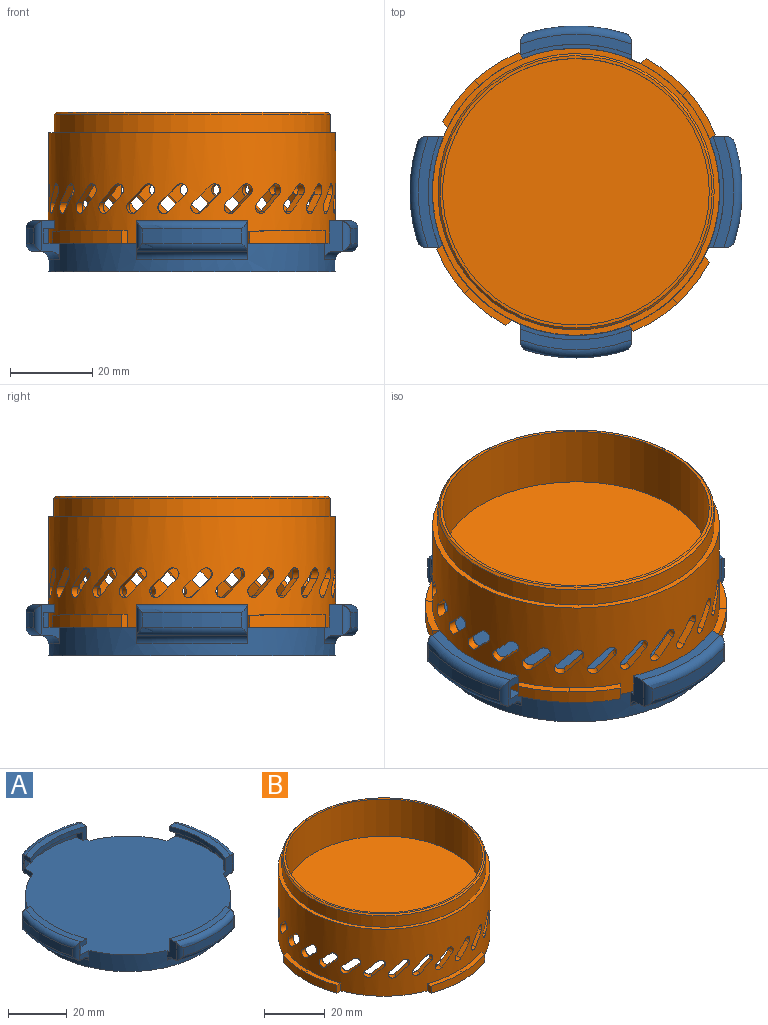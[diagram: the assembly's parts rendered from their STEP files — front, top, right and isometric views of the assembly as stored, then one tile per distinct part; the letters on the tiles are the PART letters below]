
ASSEMBLY  parts=2 mates=1
PART A: 62 faces, bbox 87.7x87.7x12.5 mm
  f0: cylinder r=35mm len=70mm, axis (0,0,-1), area 1095.9mm2, adj f1,f3,f7,f8,f19,f21,f22,f33
  f1: plane 77.24x77.24mm, normal (0,0,1), area 4232.4mm2, adj f0,f7,f8,f10,f11,f12,f21,f22
  f2: cylinder r=33.75mm len=67.5mm, axis (0,0,-1), area 954.3mm2, adj f4,f5
  f3: plane 70x70mm, normal (0,0,-1), area 163.2mm2, adj f0,f5
  f4: plane 67.5x67.5mm, normal (0,0,-1), area 3578.5mm2, adj f2
  f5: cone r=34.25mm half-angle=45deg, axis (0,0,-1), area 151.1mm2, adj f2,f3
  f6: cylinder r=40.5mm len=24.2mm, axis (0,0,1), area 86mm2, adj f15,f16,f17,f18
  f7: plane 9.51x4.46mm, normal (0,-1,0), area 18.4mm2, adj f0,f1,f9,f10,f12,f13,f14,f15
  f8: plane 9.51x4.46mm, normal (0,1,0), area 28mm2, adj f0,f1,f9,f12,f13,f15,f16,f18
  f9: plane 27x4.05mm, normal (0,0,-1), area 41.4mm2, adj f7,f8,f15,f19
  f10: cylinder r=38.62mm len=25.5mm, axis (0,0,-1), area 91mm2, adj f1,f7,f11,f14
  f11: plane 3.5x2.71mm, normal (0,-1,0), area 9.5mm2, adj f1,f10,f12,f14
  f12: cylinder r=36.06mm len=27mm, axis (0,0,-1), area 61mm2, adj f1,f7,f8,f11,f13,f14
  f13: plane 27x5.07mm, normal (0,0,1), area 67.5mm2, adj f7,f8,f12,f18
  f14: plane 25.5x5.19mm, normal (0,0,-1), area 66.7mm2, adj f7,f10,f11,f12
  f15: torus R=38.5mm, axis (0,0,1), area 84mm2, adj f6,f7,f8,f9,f16,f17
  f16: cylinder r=2mm len=7.29mm, axis (0,0,1), area 14.4mm2, adj f6,f8,f15,f18
  f17: cylinder r=2mm len=7.29mm, axis (0,0,1), area 14.4mm2, adj f6,f7,f15,f18
  f18: torus R=38.5mm, axis (0,0,1), area 84mm2, adj f6,f7,f8,f13,f16,f17
  f19: torus R=37mm, axis (0,0,1), area 87mm2, adj f0,f7,f8,f9
  f20: cylinder r=40.5mm len=24.2mm, axis (0,0,1), area 86mm2, adj f29,f30,f31,f32
  f21: plane 9.51x4.46mm, normal (-1,0,0), area 18.4mm2, adj f0,f1,f23,f24,f26,f27,f28,f29
  f22: plane 9.51x4.46mm, normal (1,0,0), area 28mm2, adj f0,f1,f23,f26,f27,f29,f30,f32
  f23: plane 27x4.05mm, normal (0,0,-1), area 41.4mm2, adj f21,f22,f29,f33
  f24: cylinder r=38.62mm len=25.5mm, axis (0,0,-1), area 91mm2, adj f1,f21,f25,f28
  f25: plane 3.5x2.71mm, normal (-1,0,0), area 9.5mm2, adj f1,f24,f26,f28
  f26: cylinder r=36.06mm len=27mm, axis (0,0,-1), area 61mm2, adj f1,f21,f22,f25,f27,f28
  f27: plane 27x5.07mm, normal (0,0,1), area 67.5mm2, adj f21,f22,f26,f32
  f28: plane 25.5x5.19mm, normal (0,0,-1), area 66.7mm2, adj f21,f24,f25,f26
  f29: torus R=38.5mm, axis (0,0,1), area 84mm2, adj f20,f21,f22,f23,f30,f31
  f30: cylinder r=2mm len=7.29mm, axis (0,0,1), area 14.4mm2, adj f20,f22,f29,f32
  f31: cylinder r=2mm len=7.29mm, axis (0,0,1), area 14.4mm2, adj f20,f21,f29,f32
  f32: torus R=38.5mm, axis (0,0,1), area 84mm2, adj f20,f21,f22,f27,f30,f31
  f33: torus R=37mm, axis (0,0,1), area 87mm2, adj f0,f21,f22,f23
  f34: cylinder r=40.5mm len=24.2mm, axis (0,0,1), area 86mm2, adj f43,f44,f45,f46
  f35: plane 9.51x4.46mm, normal (0,1,0), area 18.4mm2, adj f0,f1,f37,f38,f40,f41,f42,f43
  f36: plane 9.51x4.46mm, normal (0,-1,0), area 28mm2, adj f0,f1,f37,f40,f41,f43,f44,f46
  f37: plane 27x4.05mm, normal (0,0,-1), area 41.4mm2, adj f35,f36,f43,f47
  f38: cylinder r=38.62mm len=25.5mm, axis (0,0,-1), area 91mm2, adj f1,f35,f39,f42
  f39: plane 3.5x2.71mm, normal (0,1,0), area 9.5mm2, adj f1,f38,f40,f42
  f40: cylinder r=36.06mm len=27mm, axis (0,0,-1), area 61mm2, adj f1,f35,f36,f39,f41,f42
  f41: plane 27x5.07mm, normal (0,0,1), area 67.5mm2, adj f35,f36,f40,f46
  f42: plane 25.5x5.19mm, normal (0,0,-1), area 66.7mm2, adj f35,f38,f39,f40
  f43: torus R=38.5mm, axis (0,0,1), area 84mm2, adj f34,f35,f36,f37,f44,f45
  f44: cylinder r=2mm len=7.29mm, axis (0,0,1), area 14.4mm2, adj f34,f36,f43,f46
  f45: cylinder r=2mm len=7.29mm, axis (0,0,1), area 14.4mm2, adj f34,f35,f43,f46
  f46: torus R=38.5mm, axis (0,0,1), area 84mm2, adj f34,f35,f36,f41,f44,f45
  f47: torus R=37mm, axis (0,0,1), area 87mm2, adj f0,f35,f36,f37
  f48: cylinder r=40.5mm len=24.2mm, axis (0,0,1), area 86mm2, adj f57,f58,f59,f60
  f49: plane 9.51x4.46mm, normal (1,0,0), area 18.4mm2, adj f0,f1,f51,f52,f54,f55,f56,f57
  f50: plane 9.51x4.46mm, normal (-1,0,0), area 28mm2, adj f0,f1,f51,f54,f55,f57,f58,f60
  f51: plane 27x4.05mm, normal (0,0,-1), area 41.4mm2, adj f49,f50,f57,f61
  f52: cylinder r=38.62mm len=25.5mm, axis (0,0,-1), area 91mm2, adj f1,f49,f53,f56
  f53: plane 3.5x2.71mm, normal (1,0,0), area 9.5mm2, adj f1,f52,f54,f56
  f54: cylinder r=36.06mm len=27mm, axis (0,0,-1), area 61mm2, adj f1,f49,f50,f53,f55,f56
  f55: plane 27x5.07mm, normal (0,0,1), area 67.5mm2, adj f49,f50,f54,f60
  f56: plane 25.5x5.19mm, normal (0,0,-1), area 66.7mm2, adj f49,f52,f53,f54
  f57: torus R=38.5mm, axis (0,0,1), area 84mm2, adj f48,f49,f50,f51,f58,f59
  f58: cylinder r=2mm len=7.29mm, axis (0,0,1), area 14.4mm2, adj f48,f50,f57,f60
  f59: cylinder r=2mm len=7.29mm, axis (0,0,1), area 14.4mm2, adj f48,f49,f57,f60
  f60: torus R=38.5mm, axis (0,0,1), area 84mm2, adj f48,f49,f50,f55,f58,f59
  f61: torus R=37mm, axis (0,0,1), area 87mm2, adj f0,f49,f50,f51
PART B: 138 faces, bbox 73.5x73.5x32 mm
  f0: cylinder r=35mm len=70mm, axis (0,0,-1), area 4937.3mm2, adj f5,f8,f11,f12,f13,f14,f16,f17
  f1: plane 66.38x66.38mm, normal (0,0,1), area 142.4mm2, adj f2,f6
  f2: cylinder r=32.5mm len=65mm, axis (0,0,-1), area 3063.1mm2, adj f1,f3
  f3: plane 65x65mm, normal (0,0,1), area 3318.3mm2, adj f2
  f4: cylinder r=33.69mm len=67.38mm, axis (0,0,1), area 952.6mm2, adj f5,f6
  f5: plane 70x70mm, normal (0,0,1), area 282.7mm2, adj f0,f4
  f6: cone r=33.19mm half-angle=45deg, axis (0,0,-1), area 148.6mm2, adj f1,f4
  f7: cylinder r=33mm len=66mm, axis (0,0,1), area 2432.3mm2, adj f8,f9,f26,f27,f28,f29,f30,f31
  f8: plane 73.5x73.5mm, normal (0,0,-1), area 606mm2, adj f0,f7,f10,f11,f12,f14,f15,f16
  f9: plane 66x66mm, normal (0,0,-1), area 3421.2mm2, adj f7
  f10: cylinder r=36.75mm len=25mm, axis (0,0,-1), area 79.7mm2, adj f8,f11,f12,f13,f134
  f11: plane 2.9x1.87mm, normal (-1,0,0), area 5.4mm2, adj f0,f8,f10,f134
  f12: plane 3.2x1.87mm, normal (1,0,0), area 6mm2, adj f0,f8,f10,f13
  f13: plane 12.5x4.06mm, normal (0,0,1), area 22.3mm2, adj f0,f10,f12,f134
  f14: plane 3.2x1.87mm, normal (0,-1,0), area 6mm2, adj f0,f8,f15,f17
  f15: cylinder r=36.75mm len=25mm, axis (0,0,-1), area 79.7mm2, adj f8,f14,f16,f17,f137
  f16: plane 2.9x1.87mm, normal (0,1,0), area 5.4mm2, adj f0,f8,f15,f137
  f17: plane 12.5x4.06mm, normal (0,0,1), area 22.3mm2, adj f0,f14,f15,f137
  f18: plane 3.2x1.87mm, normal (-1,0,0), area 6mm2, adj f0,f8,f19,f21
  f19: cylinder r=36.75mm len=25mm, axis (0,0,-1), area 79.7mm2, adj f8,f18,f20,f21,f136
  f20: plane 2.9x1.87mm, normal (1,0,0), area 5.4mm2, adj f0,f8,f19,f136
  f21: plane 12.5x4.06mm, normal (0,0,1), area 22.3mm2, adj f0,f18,f19,f136
  f22: plane 3.2x1.87mm, normal (0,1,0), area 6mm2, adj f0,f8,f23,f25
  f23: cylinder r=36.75mm len=25mm, axis (0,0,-1), area 79.7mm2, adj f8,f22,f24,f25,f135
  f24: plane 2.9x1.87mm, normal (0,-1,0), area 5.4mm2, adj f0,f8,f23,f135
  f25: plane 12.5x4.06mm, normal (0,0,1), area 22.3mm2, adj f0,f22,f23,f135
  f26: cylinder r=1.5mm len=2.56mm, axis (0,-1,0), area 9.4mm2, adj f0,f7,f27,f29
  f27: plane 4.18x4.18mm, normal (0.71,0,0.71), area 11.8mm2, adj f0,f7,f26,f28
  f28: cylinder r=1.5mm len=2.62mm, axis (0,-1,0), area 9.7mm2, adj f0,f7,f27,f29
  f29: plane 4.26x4.26mm, normal (-0.71,0,-0.71), area 12.1mm2, adj f0,f7,f26,f28
  f30: cylinder r=1.5mm len=2.95mm, axis (-0.23,-0.97,0), area 9.4mm2, adj f0,f7,f31,f33
  f31: plane 4.5x4.18mm, normal (0.69,-0.16,0.71), area 11.8mm2, adj f0,f7,f30,f32
  f32: cylinder r=1.5mm len=3.1mm, axis (-0.23,-0.97,0), area 9.7mm2, adj f0,f7,f31,f33
  f33: plane 4.51x4.26mm, normal (-0.69,0.16,-0.71), area 12.1mm2, adj f0,f7,f30,f32
  f34: cylinder r=1.5mm len=3.19mm, axis (-0.45,-0.89,0), area 9.4mm2, adj f0,f7,f35,f37
  f35: plane 4.58x4.18mm, normal (0.63,-0.32,0.71), area 11.8mm2, adj f0,f7,f34,f36
  f36: cylinder r=1.5mm len=3.41mm, axis (-0.45,-0.89,0), area 9.7mm2, adj f0,f7,f35,f37
  f37: plane 4.53x4.26mm, normal (-0.63,0.32,-0.71), area 12.1mm2, adj f0,f7,f34,f36
  f38: cylinder r=1.5mm len=3.25mm, axis (-0.64,-0.77,0), area 9.4mm2, adj f0,f7,f39,f41
  f39: plane 4.41x4.32mm, normal (0.54,-0.45,0.71), area 11.8mm2, adj f0,f7,f38,f40
  f40: cylinder r=1.5mm len=3.53mm, axis (-0.64,-0.77,0), area 9.7mm2, adj f0,f7,f39,f41
  f41: plane 4.59x4.3mm, normal (-0.54,0.45,-0.71), area 12.1mm2, adj f0,f7,f38,f40
  f42: cylinder r=1.5mm len=3.25mm, axis (-0.8,-0.6,0), area 9.4mm2, adj f0,f7,f43,f45
  f43: plane 4.63x4.18mm, normal (0.42,-0.57,0.71), area 11.8mm2, adj f0,f7,f42,f44
  f44: cylinder r=1.5mm len=3.52mm, axis (-0.8,-0.6,0), area 9.7mm2, adj f0,f7,f43,f45
  f45: plane 4.86x4.26mm, normal (-0.42,0.57,-0.71), area 12.1mm2, adj f0,f7,f42,f44
  f46: cylinder r=1.5mm len=3.14mm, axis (-0.92,-0.4,0), area 9.4mm2, adj f0,f7,f47,f49
  f47: plane 4.69x4.18mm, normal (0.28,-0.65,0.71), area 11.8mm2, adj f0,f7,f46,f48
  f48: cylinder r=1.5mm len=3.35mm, axis (-0.92,-0.4,0), area 9.7mm2, adj f0,f7,f47,f49
  f49: plane 4.86x4.26mm, normal (-0.28,0.65,-0.71), area 12.1mm2, adj f0,f7,f46,f48
  f50: cylinder r=1.5mm len=2.87mm, axis (-0.98,-0.17,0), area 9.4mm2, adj f0,f7,f51,f53
  f51: plane 4.49x4.18mm, normal (0.12,-0.7,0.71), area 11.8mm2, adj f0,f7,f50,f52
  f52: cylinder r=1.5mm len=2.99mm, axis (-0.98,-0.17,0), area 9.7mm2, adj f0,f7,f51,f53
  f53: plane 4.61x4.26mm, normal (-0.12,0.7,-0.71), area 12.1mm2, adj f0,f7,f50,f52
  f54: cylinder r=1.5mm len=2.67mm, axis (-1,0.06,0), area 9.4mm2, adj f0,f7,f55,f57
  f55: plane 4.29x4.18mm, normal (-0.04,-0.71,0.71), area 11.8mm2, adj f0,f7,f54,f56
  f56: cylinder r=1.5mm len=2.76mm, axis (-1,0.06,0), area 9.7mm2, adj f0,f7,f55,f57
  f57: plane 4.34x4.26mm, normal (0.04,0.71,-0.71), area 12.1mm2, adj f0,f7,f54,f56
  f58: cylinder r=1.5mm len=3.03mm, axis (-0.96,0.29,0), area 9.4mm2, adj f0,f7,f59,f61
  f59: plane 4.55x4.18mm, normal (-0.2,-0.68,0.71), area 11.8mm2, adj f0,f7,f58,f60
  f60: cylinder r=1.5mm len=3.19mm, axis (-0.96,0.29,0), area 9.7mm2, adj f0,f7,f59,f61
  f61: plane 4.54x4.26mm, normal (0.2,0.68,-0.71), area 12.1mm2, adj f0,f7,f58,f60
  f62: cylinder r=1.5mm len=3.22mm, axis (-0.87,0.5,0), area 9.4mm2, adj f0,f7,f63,f65
  f63: plane 4.56x4.18mm, normal (-0.35,-0.61,0.71), area 11.8mm2, adj f0,f7,f62,f64
  f64: cylinder r=1.5mm len=3.45mm, axis (-0.87,0.5,0), area 9.7mm2, adj f0,f7,f63,f65
  f65: plane 4.49x4.26mm, normal (0.35,0.61,-0.71), area 12.1mm2, adj f0,f7,f62,f64
  f66: cylinder r=1.5mm len=3.24mm, axis (-0.73,0.69,0), area 9.4mm2, adj f0,f7,f67,f69
  f67: plane 4.42x4.33mm, normal (-0.49,-0.51,0.71), area 11.8mm2, adj f0,f7,f66,f68
  f68: cylinder r=1.5mm len=3.53mm, axis (-0.73,0.69,0), area 9.7mm2, adj f0,f7,f67,f69
  f69: plane 4.68x4.26mm, normal (0.49,0.51,-0.71), area 12.1mm2, adj f0,f7,f66,f68
  f70: cylinder r=1.5mm len=3.24mm, axis (-0.55,0.84,0), area 9.4mm2, adj f0,f7,f71,f73
  f71: plane 4.67x4.18mm, normal (-0.59,-0.39,0.71), area 11.8mm2, adj f0,f7,f70,f72
  f72: cylinder r=1.5mm len=3.49mm, axis (-0.55,0.84,0), area 9.7mm2, adj f0,f7,f71,f73
  f73: plane 4.88x4.26mm, normal (0.59,0.39,-0.71), area 12.1mm2, adj f0,f7,f70,f72
  f74: cylinder r=1.5mm len=3.09mm, axis (-0.34,0.94,0), area 9.4mm2, adj f0,f7,f75,f77
  f75: plane 4.66x4.18mm, normal (-0.66,-0.24,0.71), area 11.8mm2, adj f0,f7,f74,f76
  f76: cylinder r=1.5mm len=3.27mm, axis (-0.34,0.94,0), area 9.7mm2, adj f0,f7,f75,f77
  f77: plane 4.83x4.26mm, normal (0.66,0.24,-0.71), area 12.1mm2, adj f0,f7,f74,f76
  f78: cylinder r=1.5mm len=2.78mm, axis (-0.12,0.99,0), area 9.4mm2, adj f0,f7,f79,f81
  f79: plane 4.4x4.18mm, normal (-0.7,-0.08,0.71), area 11.8mm2, adj f0,f7,f78,f80
  f80: cylinder r=1.5mm len=2.88mm, axis (-0.12,0.99,0), area 9.7mm2, adj f0,f7,f79,f81
  f81: plane 4.51x4.26mm, normal (0.7,0.08,-0.71), area 12.1mm2, adj f0,f7,f78,f80
  f82: cylinder r=1.5mm len=2.78mm, axis (0.12,0.99,0), area 9.4mm2, adj f0,f7,f83,f85
  f83: plane 4.37x4.18mm, normal (-0.7,0.08,0.71), area 11.8mm2, adj f0,f7,f82,f84
  f84: cylinder r=1.5mm len=2.88mm, axis (0.12,0.99,0), area 9.7mm2, adj f0,f7,f83,f85
  f85: plane 4.41x4.26mm, normal (0.7,-0.08,-0.71), area 12.1mm2, adj f0,f7,f82,f84
  f86: cylinder r=1.5mm len=3.09mm, axis (0.34,0.94,0), area 9.4mm2, adj f0,f7,f87,f89
  f87: plane 4.57x4.18mm, normal (-0.66,0.24,0.71), area 11.8mm2, adj f0,f7,f86,f88
  f88: cylinder r=1.5mm len=3.27mm, axis (0.34,0.94,0), area 9.7mm2, adj f0,f7,f87,f89
  f89: plane 4.55x4.26mm, normal (0.66,-0.24,-0.71), area 12.1mm2, adj f0,f7,f86,f88
  f90: cylinder r=1.5mm len=3.24mm, axis (0.55,0.84,0), area 9.4mm2, adj f0,f7,f91,f93
  f91: plane 4.53x4.18mm, normal (-0.59,0.39,0.71), area 11.8mm2, adj f0,f7,f90,f92
  f92: cylinder r=1.5mm len=3.49mm, axis (0.55,0.84,0), area 9.7mm2, adj f0,f7,f91,f93
  f93: plane 4.44x4.36mm, normal (0.59,-0.39,-0.71), area 12.1mm2, adj f0,f7,f90,f92
  f94: cylinder r=1.5mm len=3.24mm, axis (0.73,0.69,0), area 9.4mm2, adj f0,f7,f95,f97
  f95: plane 4.51x4.24mm, normal (-0.49,0.51,0.71), area 11.8mm2, adj f0,f7,f94,f96
  f96: cylinder r=1.5mm len=3.53mm, axis (0.73,0.69,0), area 9.7mm2, adj f0,f7,f95,f97
  f97: plane 4.76x4.26mm, normal (0.49,-0.51,-0.71), area 12.1mm2, adj f0,f7,f94,f96
  f98: cylinder r=1.5mm len=3.22mm, axis (0.87,0.5,0), area 9.4mm2, adj f0,f7,f99,f101
  f99: plane 4.69x4.18mm, normal (-0.35,0.61,0.71), area 11.8mm2, adj f0,f7,f98,f100
  f100: cylinder r=1.5mm len=3.45mm, axis (0.87,0.5,0), area 9.7mm2, adj f0,f7,f99,f101
  f101: plane 4.89x4.26mm, normal (0.35,-0.61,-0.71), area 12.1mm2, adj f0,f7,f98,f100
  f102: cylinder r=1.5mm len=3.03mm, axis (0.96,0.29,0), area 9.4mm2, adj f0,f7,f103,f105
  f103: plane 4.62x4.18mm, normal (-0.2,0.68,0.71), area 11.8mm2, adj f0,f7,f102,f104
  f104: cylinder r=1.5mm len=3.19mm, axis (0.96,0.29,0), area 9.7mm2, adj f0,f7,f103,f105
  f105: plane 4.77x4.26mm, normal (0.2,-0.68,-0.71), area 12.1mm2, adj f0,f7,f102,f104
  f106: cylinder r=1.5mm len=2.67mm, axis (1,0.06,0), area 9.4mm2, adj f0,f7,f107,f109
  f107: plane 4.3x4.18mm, normal (-0.04,0.71,0.71), area 11.8mm2, adj f0,f7,f106,f108
  f108: cylinder r=1.5mm len=2.76mm, axis (1,0.06,0), area 9.7mm2, adj f0,f7,f107,f109
  f109: plane 4.39x4.26mm, normal (0.04,-0.71,-0.71), area 12.1mm2, adj f0,f7,f106,f108
  f110: cylinder r=1.5mm len=2.87mm, axis (0.98,-0.17,0), area 9.4mm2, adj f0,f7,f111,f113
  f111: plane 4.45x4.18mm, normal (0.12,0.7,0.71), area 11.8mm2, adj f0,f7,f110,f112
  f112: cylinder r=1.5mm len=2.99mm, axis (0.98,-0.17,0), area 9.7mm2, adj f0,f7,f111,f113
  f113: plane 4.47x4.26mm, normal (-0.12,-0.7,-0.71), area 12.1mm2, adj f0,f7,f110,f112
  f114: cylinder r=1.5mm len=3.14mm, axis (0.92,-0.4,0), area 9.4mm2, adj f0,f7,f115,f117
  f115: plane 4.59x4.18mm, normal (0.28,0.65,0.71), area 11.8mm2, adj f0,f7,f114,f116
  f116: cylinder r=1.5mm len=3.35mm, axis (0.92,-0.4,0), area 9.7mm2, adj f0,f7,f115,f117
  f117: plane 4.55x4.26mm, normal (-0.28,-0.65,-0.71), area 12.1mm2, adj f0,f7,f114,f116
  f118: cylinder r=1.5mm len=3.25mm, axis (0.8,-0.6,0), area 9.4mm2, adj f0,f7,f119,f121
  f119: plane 4.48x4.21mm, normal (0.42,0.57,0.71), area 11.8mm2, adj f0,f7,f118,f120
  f120: cylinder r=1.5mm len=3.52mm, axis (0.8,-0.6,0), area 9.7mm2, adj f0,f7,f119,f121
  f121: plane 4.48x4.38mm, normal (-0.42,-0.57,-0.71), area 12.1mm2, adj f0,f7,f118,f120
  f122: cylinder r=1.5mm len=3.25mm, axis (0.64,-0.77,0), area 9.4mm2, adj f0,f7,f123,f125
  f123: plane 4.58x4.18mm, normal (0.54,0.45,0.71), area 11.8mm2, adj f0,f7,f122,f124
  f124: cylinder r=1.5mm len=3.53mm, axis (0.64,-0.77,0), area 9.7mm2, adj f0,f7,f123,f125
  f125: plane 4.81x4.26mm, normal (-0.54,-0.45,-0.71), area 12.1mm2, adj f0,f7,f122,f124
  f126: cylinder r=1.5mm len=3.19mm, axis (0.45,-0.89,0), area 9.4mm2, adj f0,f7,f127,f129
  f127: plane 4.7x4.18mm, normal (0.63,0.32,0.71), area 11.8mm2, adj f0,f7,f126,f128
  f128: cylinder r=1.5mm len=3.41mm, axis (0.45,-0.89,0), area 9.7mm2, adj f0,f7,f127,f129
  f129: plane 4.89x4.26mm, normal (-0.63,-0.32,-0.71), area 12.1mm2, adj f0,f7,f126,f128
  f130: cylinder r=1.5mm len=2.95mm, axis (0.23,-0.97,0), area 9.4mm2, adj f0,f7,f131,f133
  f131: plane 4.56x4.18mm, normal (0.69,0.16,0.71), area 11.8mm2, adj f0,f7,f130,f132
  f132: cylinder r=1.5mm len=3.1mm, axis (0.23,-0.97,0), area 9.7mm2, adj f0,f7,f131,f133
  f133: plane 4.7x4.26mm, normal (-0.69,-0.16,-0.71), area 12.1mm2, adj f0,f7,f130,f132
  f134: plane 12.51x4.06mm, normal (-0.02,0,1), area 22.4mm2, adj f0,f10,f11,f13
  f135: plane 12.51x4.06mm, normal (0,-0.02,1), area 22.4mm2, adj f0,f23,f24,f25
  f136: plane 12.51x4.06mm, normal (0.02,0,1), area 22.4mm2, adj f0,f19,f20,f21
  f137: plane 12.51x4.06mm, normal (0,0.02,1), area 22.4mm2, adj f0,f15,f16,f17
PLACE A t=(0,0,-17)mm fixed
PLACE B rot(axis=(0,0,1),42.3deg) t=(0,0,17)mm
MATE revolute B.f0 <-> A.f2  axis (0,0,-1) through (0,0,0)mm
